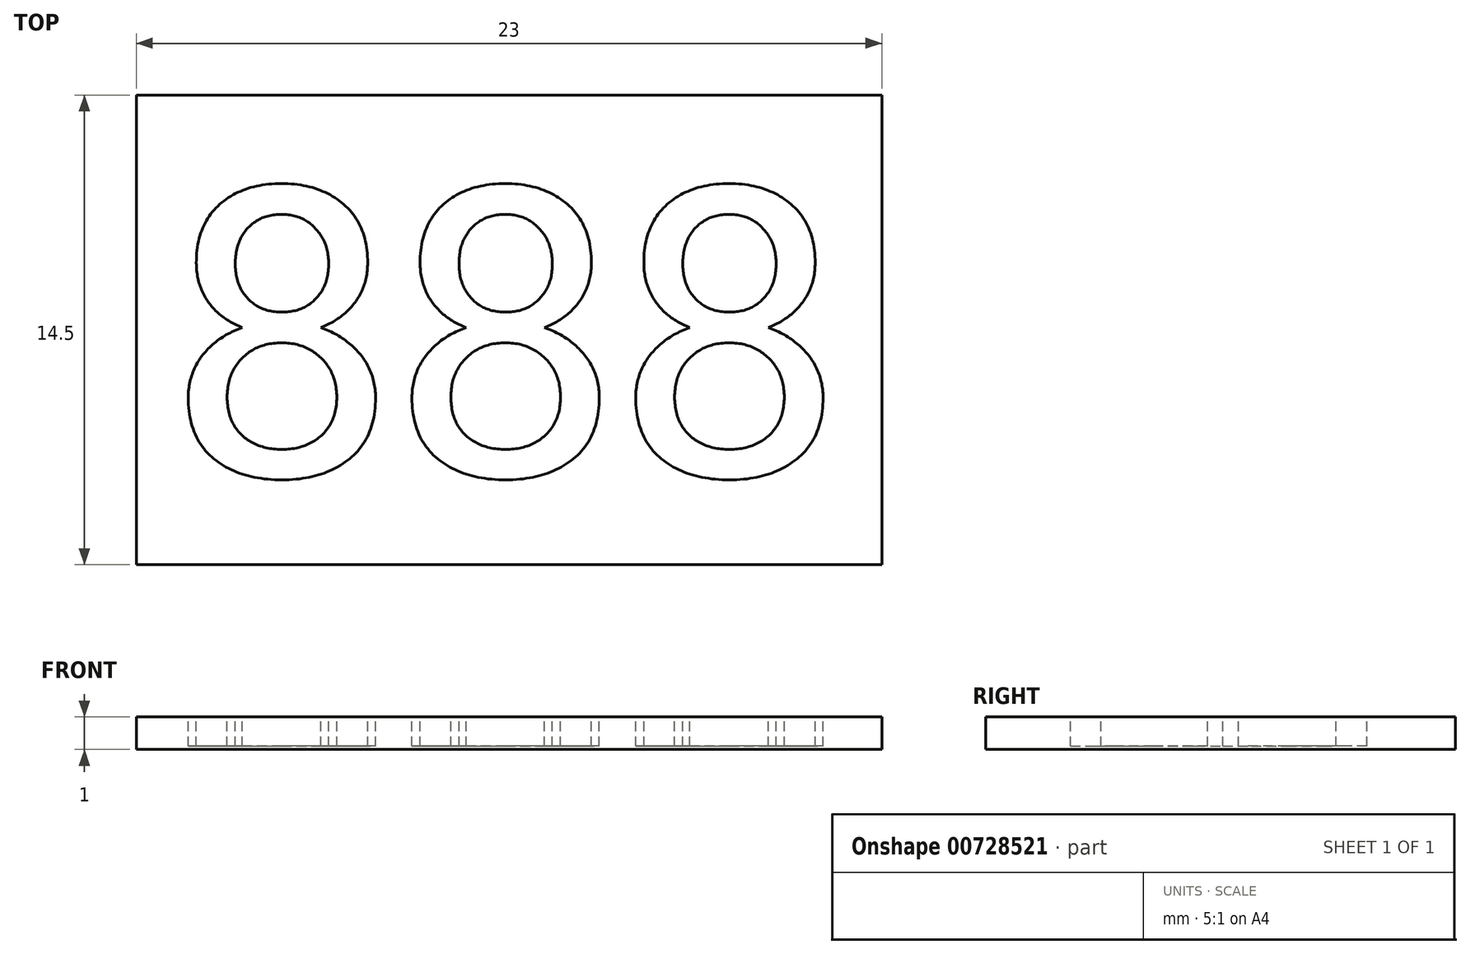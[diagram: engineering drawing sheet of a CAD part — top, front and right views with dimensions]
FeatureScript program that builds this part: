
annotation { "Feature Type Name" : "Feature", "Feature Type Description" : "" }
export const myFeature = defineFeature(function(context is Context, id is Id, definition is map)
    precondition{}
    {
        {
            var Q0;
            Q0=qCreatedBy(makeId("Top.planeOp"),FACE);
            var sketch = newSketch(context, id + "F0", { "sketchPlane" : qUnion([Q0])});
            skLineSegment(sketch, "E0.bottom", {"start": v(-23, 0) * mm, "end": v(0, 0) * mm});
            skLineSegment(sketch, "E0.top", {"start": v(-23, 14.5) * mm, "end": v(0, 14.5) * mm});
            skLineSegment(sketch, "E0.left", {"start": v(-23, 0) * mm, "end": v(-23, 14.5) * mm});
            skLineSegment(sketch, "E0.right", {"start": v(0, 0) * mm, "end": v(0, 14.5) * mm});
            skSolve(sketch);
        }
        {
            var Q0;
            Q0=makeQuery(id+"F0.imprint","IMPRINT",FACE,{"disambiguationData":[TD([[makeQuery(id+"F0.imprint","IMPRINT",EDGE,{"derivedFrom":sQuery(id+"F0.wireOp",EDGE,"E0.bottom")}),1.0]])]});
            extrude(context, id + "F1", {"entities" : qUnion([Q0]), "depth" : 1 * mm, "offsetDistance" : 25 * mm});
        }
        {
            var Q0;
            Q0=makeQuery(id+"F1.opExtrude","CAP_FACE",FACE,{"disambiguationData":[OSD([sQuery(id+"F0.wireOp",EDGE,"E0.bottom"),sQuery(id+"F0.wireOp",EDGE,"E0.top"),sQuery(id+"F0.wireOp",EDGE,"E0.left"),sQuery(id+"F0.wireOp",EDGE,"E0.right")])],"isStart":false});
            var sketch = newSketch(context, id + "F2", { "sketchPlane" : qUnion([Q0])});
            skText(sketch, "E1", { "text": "888", "fontName": "RobotoSlab-Regular.ttf"});
            skLineSegment(sketch, "E2", {"start": v(-11.5, 14.5) * mm, "end": v(-11.5, 0) * mm, "construction": true});
            skLineSegment(sketch, "E3", {"start": v(-23, 7.25) * mm, "end": v(0, 7.25) * mm, "construction": true});
            skLineSegment(sketch, "E4", {"start": v(-21.96, 7.25) * mm, "end": v(-1.04, 7.25) * mm, "construction": true});
            const initialGuessF2  = {"E1": [-0.02196, 0.00275, 1, 0, 0.009]};
            skSetInitialGuess(sketch, initialGuessF2);
            skSolve(sketch);
        }
        {
            var Q0;
            Q0=makeQuery(id+"F2.imprint","IMPRINT",FACE,{"disambiguationData":[TD([[makeQuery(id+"F2.imprint","IMPRINT",EDGE,{"derivedFrom":sQuery(id+"F2.wireOp",EDGE,"E1.sketch_text.stroke-64")}),-1.0]])]});
            var Q1;
            Q1=makeQuery(id+"F2.imprint","IMPRINT",FACE,{"disambiguationData":[TD([[makeQuery(id+"F2.imprint","IMPRINT",EDGE,{"derivedFrom":sQuery(id+"F2.wireOp",EDGE,"E1.sketch_text.stroke-32")}),-1.0]])]});
            var Q2;
            Q2=makeQuery(id+"F2.imprint","IMPRINT",FACE,{"disambiguationData":[TD([[makeQuery(id+"F2.imprint","IMPRINT",EDGE,{"derivedFrom":sQuery(id+"F2.wireOp",EDGE,"E1.sketch_text.stroke-0")}),-1.0]])]});
            extrude(context, id + "F3", {"entities" : qUnion([Q0, Q1, Q2]), "operationType" : NewBodyOperationType.REMOVE, "oppositeDirection" : true, "depth" : 0.9 * mm, "offsetDistance" : 25 * mm});
        }
    });
